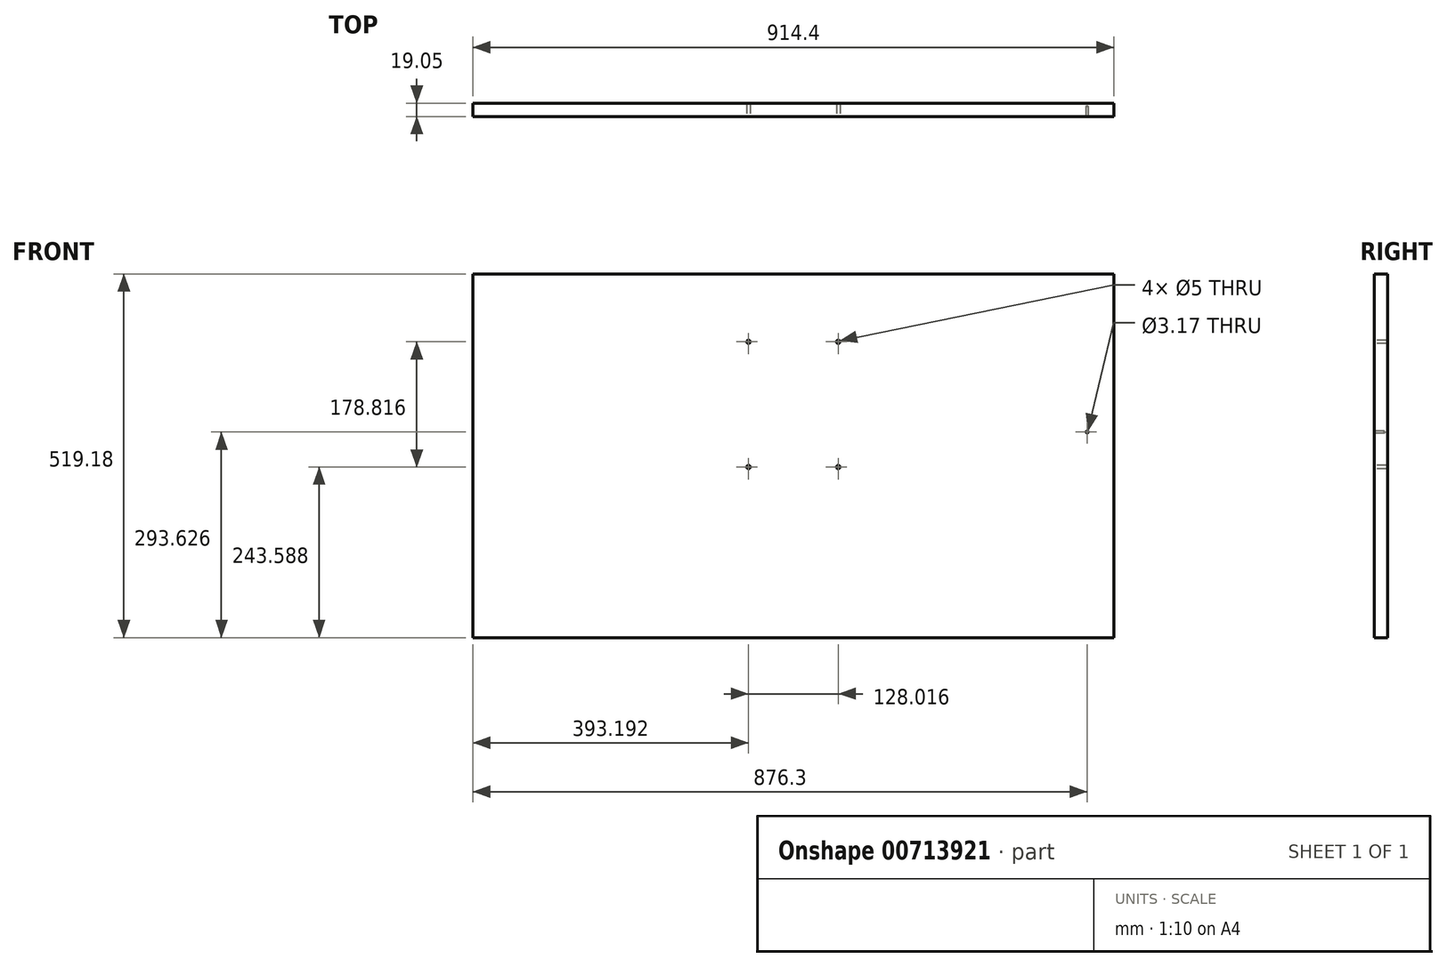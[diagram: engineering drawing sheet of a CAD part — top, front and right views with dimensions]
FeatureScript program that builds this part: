
annotation { "Feature Type Name" : "Feature", "Feature Type Description" : "" }
export const myFeature = defineFeature(function(context is Context, id is Id, definition is map)
    precondition{}
    {
        {
            var Q0;
            Q0=qCreatedBy(makeId("Front.planeOp"),FACE);
            var sketch = newSketch(context, id + "F0", { "sketchPlane" : qUnion([Q0])});
            skLineSegment(sketch, "E0.bottom", {"start": v(457.2, 259.59) * mm, "end": v(-457.2, 259.59) * mm});
            skLineSegment(sketch, "E0.top", {"start": v(457.2, -259.59) * mm, "end": v(-457.2, -259.59) * mm});
            skLineSegment(sketch, "E0.left", {"start": v(457.2, 259.59) * mm, "end": v(457.2, -259.59) * mm});
            skLineSegment(sketch, "E0.right", {"start": v(-457.2, 259.59) * mm, "end": v(-457.2, -259.59) * mm});
            skPoint(sketch, "E0.middle", {"position": v(0, 0) * mm});
            skSolve(sketch);
        }
        {
            var Q0;
            Q0=makeQuery(id+"F0.imprint","IMPRINT",FACE,{"disambiguationData":[TD([[makeQuery(id+"F0.imprint","IMPRINT",EDGE,{"derivedFrom":sQuery(id+"F0.wireOp",EDGE,"E0.bottom")}),1.0]])]});
            extrude(context, id + "F1", {"entities" : qUnion([Q0]), "depth" : 19.05 * mm, "offsetDistance" : 25.4 * mm});
        }
        {
            var Q0;
            Q0=makeQuery(id+"F1.opExtrude","CAP_FACE",FACE,{"disambiguationData":[OSD([sQuery(id+"F0.wireOp",EDGE,"E0.bottom"),sQuery(id+"F0.wireOp",EDGE,"E0.top"),sQuery(id+"F0.wireOp",EDGE,"E0.left"),sQuery(id+"F0.wireOp",EDGE,"E0.right")])],"isStart":false});
            var sketch = newSketch(context, id + "F2", { "sketchPlane" : qUnion([Q0])});
            skLineSegment(sketch, "E1", {"start": v(0, -259.59) * mm, "end": v(0, -16) * mm});
            skLineSegment(sketch, "E2", {"start": v(0, -16) * mm, "end": v(64, -16) * mm});
            skLineSegment(sketch, "E3", {"start": v(0, -16) * mm, "end": v(-64, -16) * mm});
            skLineSegment(sketch, "E4", {"start": v(0, 259.59) * mm, "end": v(0, 162.81) * mm});
            skLineSegment(sketch, "E5", {"start": v(0, 162.81) * mm, "end": v(64, 162.81) * mm});
            skLineSegment(sketch, "E6", {"start": v(0, 162.81) * mm, "end": v(-64, 162.81) * mm});
            skPoint(sketch, "E7", {"position": v(-64, -16) * mm});
            skPoint(sketch, "E8", {"position": v(64, -16) * mm});
            skPoint(sketch, "E9", {"position": v(-64, 162.81) * mm});
            skPoint(sketch, "E10", {"position": v(64, 162.81) * mm});
            skSolve(sketch);
        }
        {
            var Q0;
            Q0=sQuery(id+"F2.wireOp",VERTEX,"E9");
            var Q1;
            Q1=sQuery(id+"F2.wireOp",VERTEX,"E10");
            var Q2;
            Q2=sQuery(id+"F2.wireOp",VERTEX,"E7");
            var Q3;
            Q3=sQuery(id+"F2.wireOp",VERTEX,"E8");
            var Q4;
            Q4=makeQuery(id+"F1.opExtrude","SWEPT_BODY",BODY,{"disambiguationData":[OSD([sQuery(id+"F0.wireOp",EDGE,"E0.bottom"),sQuery(id+"F0.wireOp",EDGE,"E0.top"),sQuery(id+"F0.wireOp",EDGE,"E0.left"),sQuery(id+"F0.wireOp",EDGE,"E0.right")])]});
            hole(context, id + "F3", {"style" : HoleStyle.SIMPLE, "endStyle" : HoleEndStyle.BLIND, "holeDiameter" : 5 * mm, "majorDiameter" : 6.35 * mm, "holeDepth" : 25.4 * mm, "isTappedThrough" : true, "tappedDepth" : 12.7 * mm, "tapClearance" : 3, "startFromSketch" : true, "locations" : qUnion([Q0, Q1, Q2, Q3]), "scope" : qUnion([Q4])});
        }
        {
            var Q0;
            Q0=makeQuery(id+"F1.opExtrude","CAP_FACE",FACE,{"disambiguationData":[OSD([sQuery(id+"F0.wireOp",EDGE,"E0.bottom"),sQuery(id+"F0.wireOp",EDGE,"E0.top"),sQuery(id+"F0.wireOp",EDGE,"E0.left"),sQuery(id+"F0.wireOp",EDGE,"E0.right")])],"isStart":false});
            var sketch = newSketch(context, id + "F4", { "sketchPlane" : qUnion([Q0])});
            skLineSegment(sketch, "E11", {"start": v(457.2, -259.59) * mm, "end": v(457.2, 34.04) * mm});
            skLineSegment(sketch, "E12", {"start": v(457.2, 34.04) * mm, "end": v(419.1, 34.04) * mm});
            skPoint(sketch, "E13", {"position": v(419.1, 34.04) * mm});
            skSolve(sketch);
        }
        {
            var Q0;
            Q0=sQuery(id+"F4.wireOp",VERTEX,"E13");
            var Q1;
            Q1=makeQuery(id+"F1.opExtrude","SWEPT_BODY",BODY,{"disambiguationData":[OSD([sQuery(id+"F0.wireOp",EDGE,"E0.bottom"),sQuery(id+"F0.wireOp",EDGE,"E0.top"),sQuery(id+"F0.wireOp",EDGE,"E0.left"),sQuery(id+"F0.wireOp",EDGE,"E0.right")])]});
            hole(context, id + "F5", {"style" : HoleStyle.SIMPLE, "endStyle" : HoleEndStyle.BLIND, "holeDiameter" : 3.17 * mm, "majorDiameter" : 6.35 * mm, "holeDepth" : 14.22 * mm, "isTappedThrough" : true, "tappedDepth" : 12.7 * mm, "tapClearance" : 3, "startFromSketch" : true, "locations" : qUnion([Q0]), "scope" : qUnion([Q1])});
        }
    });
